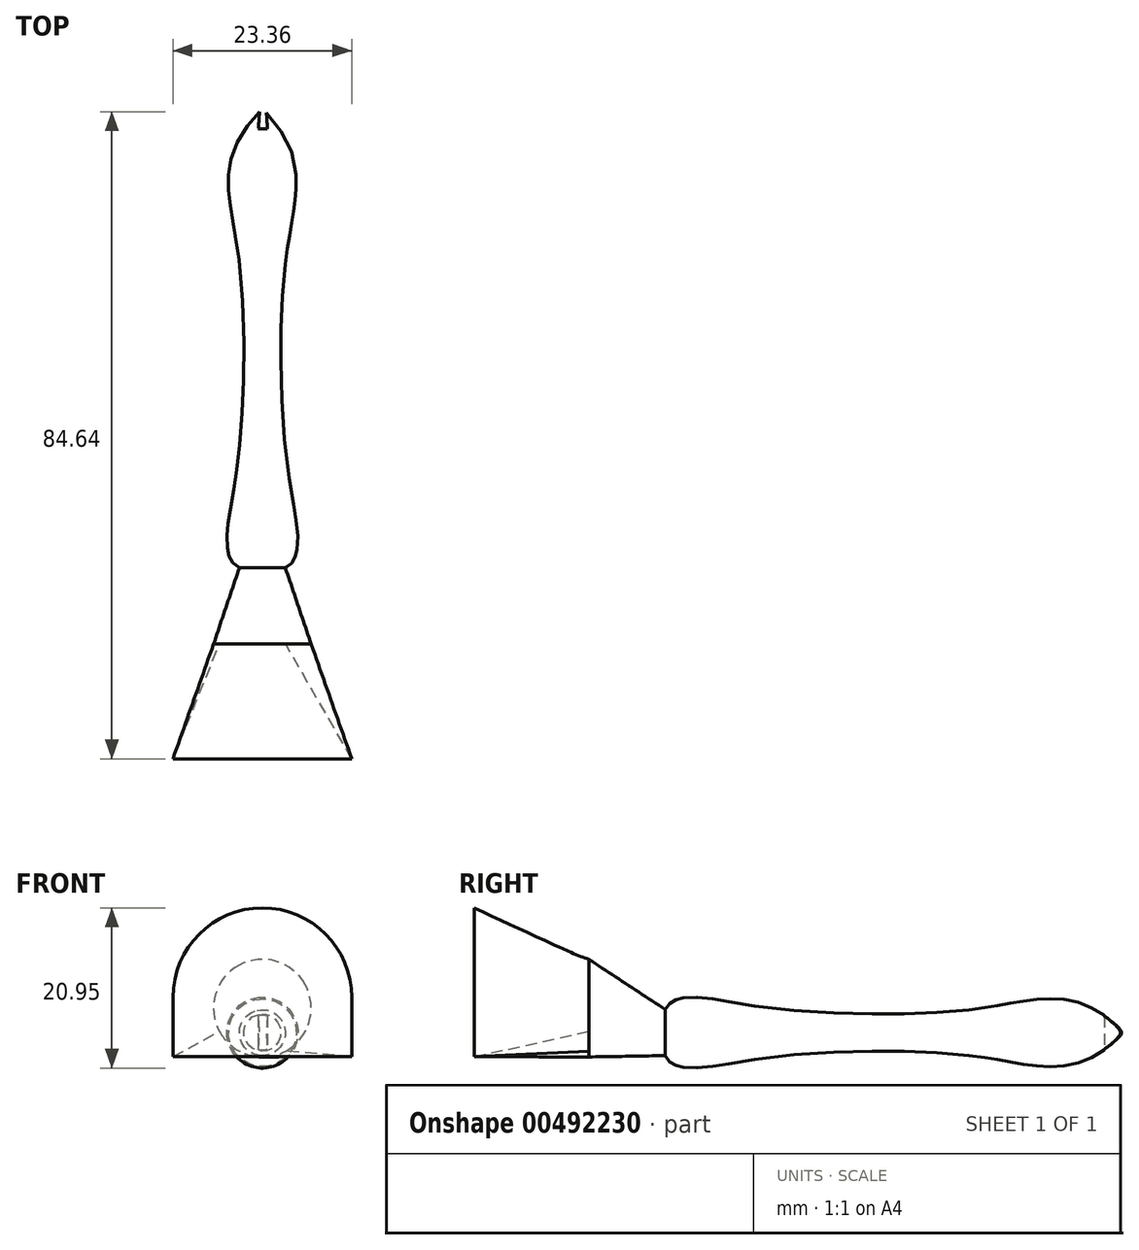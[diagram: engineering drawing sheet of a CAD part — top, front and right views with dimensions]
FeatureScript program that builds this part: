
annotation { "Feature Type Name" : "Feature", "Feature Type Description" : "" }
export const myFeature = defineFeature(function(context is Context, id is Id, definition is map)
    precondition{}
    {
        {
            var Q0;
            Q0=qCreatedBy(makeId("Right.planeOp"),FACE);
            var sketch = newSketch(context, id + "F0", { "sketchPlane" : qUnion([Q0])});
            skLineSegment(sketch, "E0", {"start": v(0, 0) * mm, "end": v(60, 0) * mm});
            skFitSpline(sketch, "E1", {"points": [v(60, 0) * mm, v(48.67, 4.36) * mm, v(38.73, 2.88) * mm, v(13.56, 3.23) * mm, v(2.58, 4.58) * mm, v(0, 3) * mm], "startDerivative": vector(-61.7, 63.72) * mm, "endDerivative": vector(-8.1, -25.92) * mm});
            skLineSegment(sketch, "E2", {"start": v(0, 3) * mm, "end": v(0, 0) * mm});
            skSolve(sketch);
        }
        {
            var Q0;
            Q0=makeQuery(id+"F0.imprint","IMPRINT",FACE,{"disambiguationData":[TD([[makeQuery(id+"F0.imprint","IMPRINT",EDGE,{"derivedFrom":sQuery(id+"F0.wireOp",EDGE,"E0")}),1.0]])]});
            var Q1;
            Q1=sQuery(id+"F0.wireOp",EDGE,"E0");
            revolve(context, id + "F1", {"entities" : qUnion([Q0]), "axis" : qUnion([Q1]), "revolveType" : RevolveType.FULL});
        }
        {
            var Q0;
            Q0=qCreatedBy(makeId("Top.planeOp"),FACE);
            var sketch = newSketch(context, id + "F2", { "sketchPlane" : qUnion([Q0])});
            skLineSegment(sketch, "E3", {"start": v(-0.53, 57.37) * mm, "end": v(0.68, 57.37) * mm});
            skLineSegment(sketch, "E4", {"start": v(0.68, 57.37) * mm, "end": v(0.42, 60.89) * mm});
            skLineSegment(sketch, "E5", {"start": v(0.42, 60.89) * mm, "end": v(-0.27, 60.84) * mm});
            skLineSegment(sketch, "E6", {"start": v(-0.27, 60.84) * mm, "end": v(-0.53, 57.37) * mm});
            skSolve(sketch);
        }
        {
            var Q0;
            Q0 = qSketchRegion(id + "F2", true);
            extrude(context, id + "F3", {"entities" : qUnion([Q0]), "operationType" : NewBodyOperationType.REMOVE, "endBound" : BoundingType.THROUGH_ALL, "depth" : 25 * mm, "hasSecondDirection" : true, "secondDirectionOppositeDirection" : true, "secondDirectionDepth" : 25 * mm});
        }
        {
            var Q0;
            Q0=qCreatedBy(makeId("Front.planeOp"),FACE);
            cPlane(context, id + "F4", {"entities" : qUnion([Q0]), "cplaneType" : CPlaneType.OFFSET, "offset" : 10 * mm, "width" : 150 * mm, "height" : 150 * mm});
        }
        {
            var Q0;
            Q0=qCreatedBy(id+"F4.planeOp",FACE);
            var sketch = newSketch(context, id + "F5", { "sketchPlane" : qUnion([Q0])});
            skCircle(sketch, "E7", {"center": v(0, 3.2) * mm, "radius": 6.38 * mm});
            skSolve(sketch);
        }
        {
            var Q1;
            Q1=makeQuery(id+"F1.opRevolve","SWEPT_FACE",FACE,{"disambiguationData":[OSD([sQuery(id+"F0.wireOp",EDGE,"E2")])]});
            var Q2;
            Q2=makeQuery(id+"F5.imprint","IMPRINT",FACE,{"disambiguationData":[TD([[makeQuery(id+"F5.imprint","IMPRINT",EDGE,{"derivedFrom":sQuery(id+"F5.wireOp",EDGE,"E7")}),1.0]])]});
            loft(context, id + "F6", {"operationType" : NewBodyOperationType.ADD, "sheetProfilesArray" : [{ "sheetProfileEntities" : qUnion([Q1]) }, { "sheetProfileEntities" : qUnion([Q2]) }]});
        }
        {
            var Q0;
            Q0=qCreatedBy(makeId("Front.planeOp"),FACE);
            cPlane(context, id + "F7", {"entities" : qUnion([Q0]), "cplaneType" : CPlaneType.OFFSET, "offset" : 25 * mm, "width" : 150 * mm, "height" : 150 * mm});
        }
        {
            var Q0;
            Q0=qCreatedBy(id+"F7.planeOp",FACE);
            var sketch = newSketch(context, id + "F8", { "sketchPlane" : qUnion([Q0])});
            skLineSegment(sketch, "E8", {"start": v(-11.68, -3.14) * mm, "end": v(-11.68, 4.64) * mm});
            skArc(sketch, "E9", {"start": v(11.68, 4.64) * mm, "mid": v(0, 16.32) * mm, "end": v(-11.68, 4.64) * mm});
            skLineSegment(sketch, "E10", {"start": v(11.68, 4.64) * mm, "end": v(11.68, -3.14) * mm});
            skLineSegment(sketch, "E11", {"start": v(-11.68, -3.14) * mm, "end": v(11.68, -3.14) * mm});
            skSolve(sketch);
        }
        {
            var Q2;
            Q2=makeQuery(id+"F8.imprint","IMPRINT",FACE,{"disambiguationData":[TD([[makeQuery(id+"F8.imprint","IMPRINT",EDGE,{"derivedFrom":sQuery(id+"F8.wireOp",EDGE,"E8")}),-1.0]])]});
            var Q3;
            Q3=makeQuery(id+"F6.opLoft","CAP_FACE",FACE,{"disambiguationData":[OSD([makeQuery(id+"F5.imprint","IMPRINT",FACE,{"disambiguationData":[TD([[makeQuery(id+"F5.imprint","IMPRINT",EDGE,{"derivedFrom":sQuery(id+"F5.wireOp",EDGE,"E7")}),1.0]])]})])],"isStart":true});
            loft(context, id + "F9", {"operationType" : NewBodyOperationType.ADD, "sheetProfilesArray" : [{ "sheetProfileEntities" : qUnion([Q2]) }, { "sheetProfileEntities" : qUnion([Q3]) }]});
        }
    });
